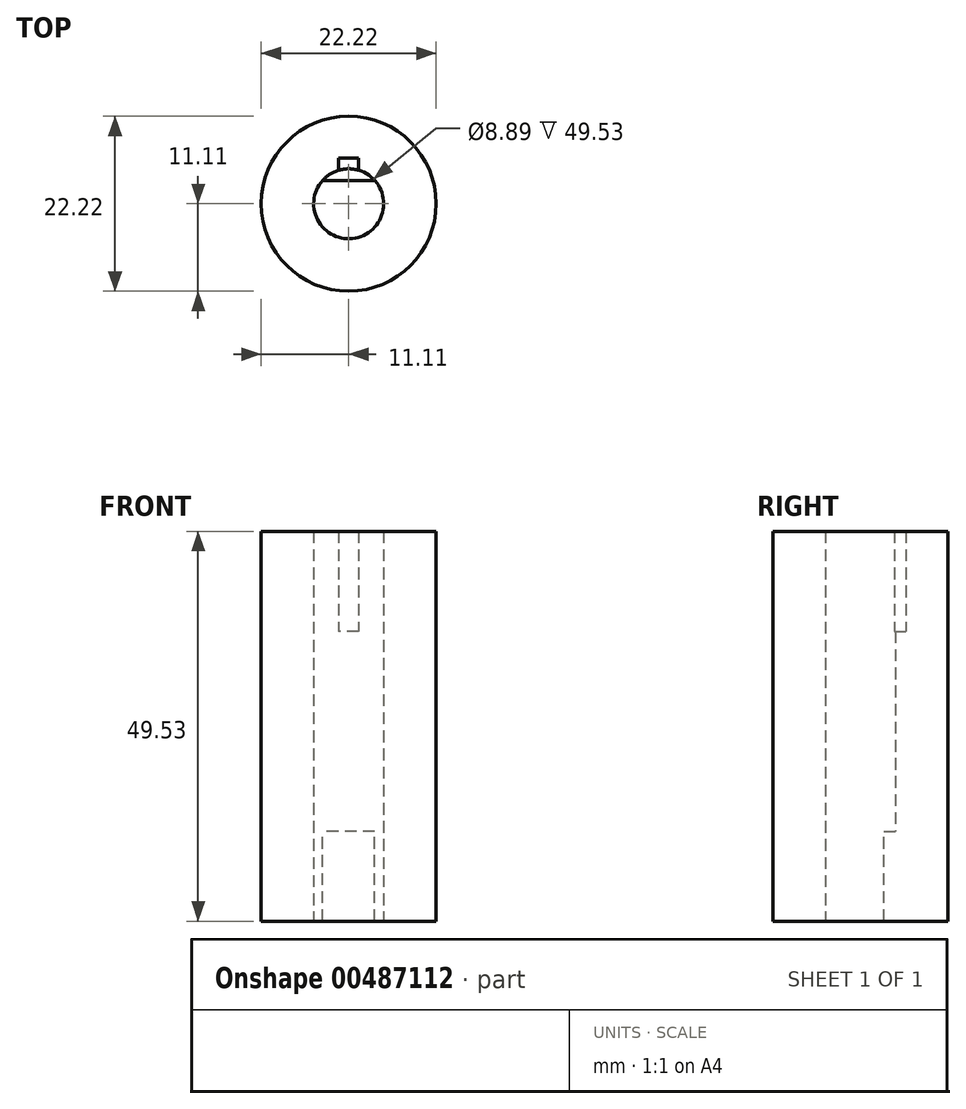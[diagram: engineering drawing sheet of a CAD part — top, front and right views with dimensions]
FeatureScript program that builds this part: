
annotation { "Feature Type Name" : "Feature", "Feature Type Description" : "" }
export const myFeature = defineFeature(function(context is Context, id is Id, definition is map)
    precondition{}
    {
        {
            var Q0;
            Q0=qCreatedBy(makeId("Top.planeOp"),FACE);
            var sketch = newSketch(context, id + "F0", { "sketchPlane" : qUnion([Q0])});
            skCircle(sketch, "E0", {"center": v(0, 0) * mm, "radius": 11.11 * mm});
            skCircle(sketch, "E1", {"center": v(0, 0) * mm, "radius": 4.45 * mm});
            skSolve(sketch);
        }
        {
            var Q0;
            Q0 = qSketchRegion(id + "F0", true);
            extrude(context, id + "F1", {"entities" : qUnion([Q0]), "depth" : 25.4 * mm});
        }
        {
            var Q0;
            Q0=makeQuery(id+"F1.opExtrude","CAP_FACE",FACE,{"disambiguationData":[OSD([sQuery(id+"F0.wireOp",EDGE,"E0"),sQuery(id+"F0.wireOp",EDGE,"E1")])],"isStart":true});
            var sketch = newSketch(context, id + "F2", { "sketchPlane" : qUnion([Q0])});
            skLineSegment(sketch, "E2", {"start": v(3.3, -2.98) * mm, "end": v(-3.3, -2.98) * mm});
            skArc(sketch, "E3", {"start": v(3.3, -2.98) * mm, "mid": v(0, 4.44) * mm, "end": v(-3.3, -2.98) * mm});
            skCircle(sketch, "E4", {"center": v(0, 0) * mm, "radius": 11.11 * mm});
            skSolve(sketch);
        }
        {
            var Q0;
            Q0 = qSketchRegion(id + "F2", true);
            extrude(context, id + "F3", {"entities" : qUnion([Q0]), "operationType" : NewBodyOperationType.ADD, "depth" : 11.43 * mm});
        }
        {
            var Q0;
            Q0=makeQuery(id+"F1.opExtrude","CAP_FACE",FACE,{"disambiguationData":[OSD([sQuery(id+"F0.wireOp",EDGE,"E0"),sQuery(id+"F0.wireOp",EDGE,"E1")])],"isStart":false});
            var sketch = newSketch(context, id + "F4", { "sketchPlane" : qUnion([Q0])});
            skArc(sketch, "E5", {"start": v(-1.27, 4.26) * mm, "mid": v(0, -4.45) * mm, "end": v(1.27, 4.26) * mm});
            skLineSegment(sketch, "E6.bottom", {"start": v(1.27, -5.78) * mm, "end": v(-1.27, -5.78) * mm, "construction": true});
            skLineSegment(sketch, "E6.top", {"start": v(1.27, 5.78) * mm, "end": v(-1.27, 5.78) * mm});
            skLineSegment(sketch, "E6.left", {"start": v(1.27, -5.78) * mm, "end": v(1.27, -4.26) * mm, "construction": true});
            skLineSegment(sketch, "E6.right", {"start": v(-1.27, -5.78) * mm, "end": v(-1.27, -4.26) * mm, "construction": true});
            skPoint(sketch, "E7", {"position": v(1.27, 4.26) * mm});
            skLineSegment(sketch, "E8.trimOffspring", {"start": v(-1.27, 4.26) * mm, "end": v(-1.27, 5.78) * mm});
            skLineSegment(sketch, "E9.trimOffspring", {"start": v(1.27, 4.26) * mm, "end": v(1.27, 5.78) * mm});
            skSolve(sketch);
        }
        {
            var Q0;
            Q0=makeQuery(id+"F4.imprint","IMPRINT",FACE,{"disambiguationData":[TD([[makeQuery(id+"F4.imprint","IMPRINT",EDGE,{"derivedFrom":sQuery(id+"F4.wireOp",EDGE,"E5")}),-1.0]])]});
            extrude(context, id + "F5", {"entities" : qUnion([Q0]), "operationType" : NewBodyOperationType.ADD, "depth" : 12.7 * mm});
        }
    });
